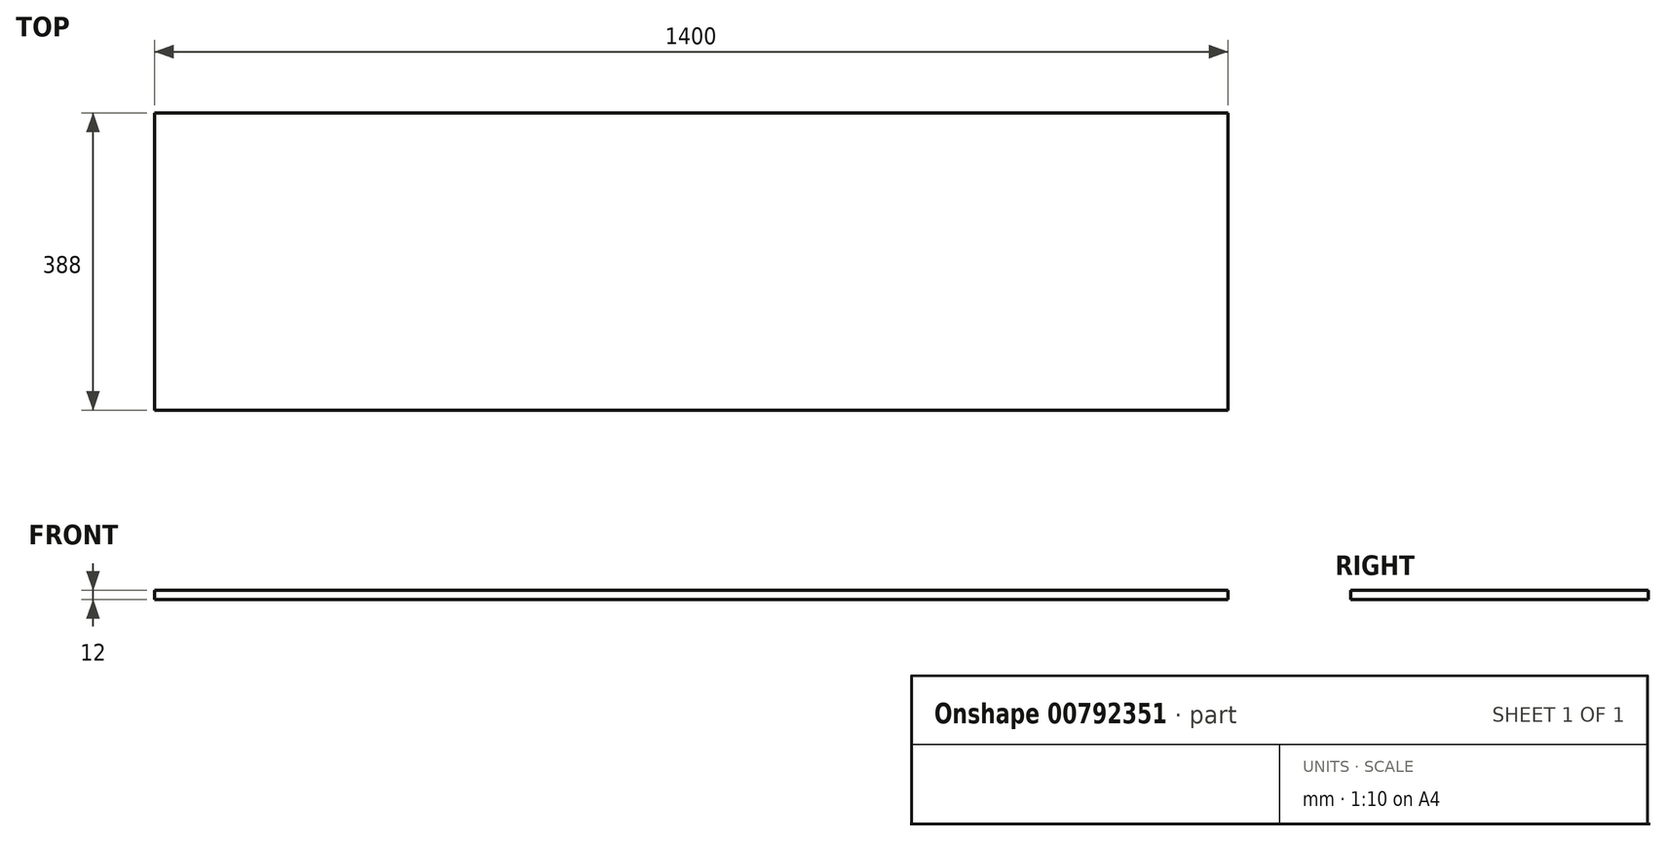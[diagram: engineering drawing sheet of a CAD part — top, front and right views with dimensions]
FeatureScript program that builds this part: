
annotation { "Feature Type Name" : "Feature", "Feature Type Description" : "" }
export const myFeature = defineFeature(function(context is Context, id is Id, definition is map)
    precondition{}
    {
        {
            var Q0;
            Q0=qCreatedBy(makeId("Top.planeOp"),FACE);
            var sketch = newSketch(context, id + "F0", { "sketchPlane" : qUnion([Q0])});
            skLineSegment(sketch, "E0.bottom", {"start": v(700, 194) * mm, "end": v(-700, 194) * mm});
            skLineSegment(sketch, "E0.top", {"start": v(700, -194) * mm, "end": v(-700, -194) * mm});
            skLineSegment(sketch, "E0.left", {"start": v(700, 194) * mm, "end": v(700, -194) * mm});
            skLineSegment(sketch, "E0.right", {"start": v(-700, 194) * mm, "end": v(-700, -194) * mm});
            skPoint(sketch, "E0.middle", {"position": v(0, 0) * mm});
            skSolve(sketch);
        }
        {
            var Q0;
            Q0 = qSketchRegion(id + "F0", true);
            extrude(context, id + "F1", {"entities" : qUnion([Q0]), "depth" : 12 * mm, "offsetDistance" : 25 * mm});
        }
    });
